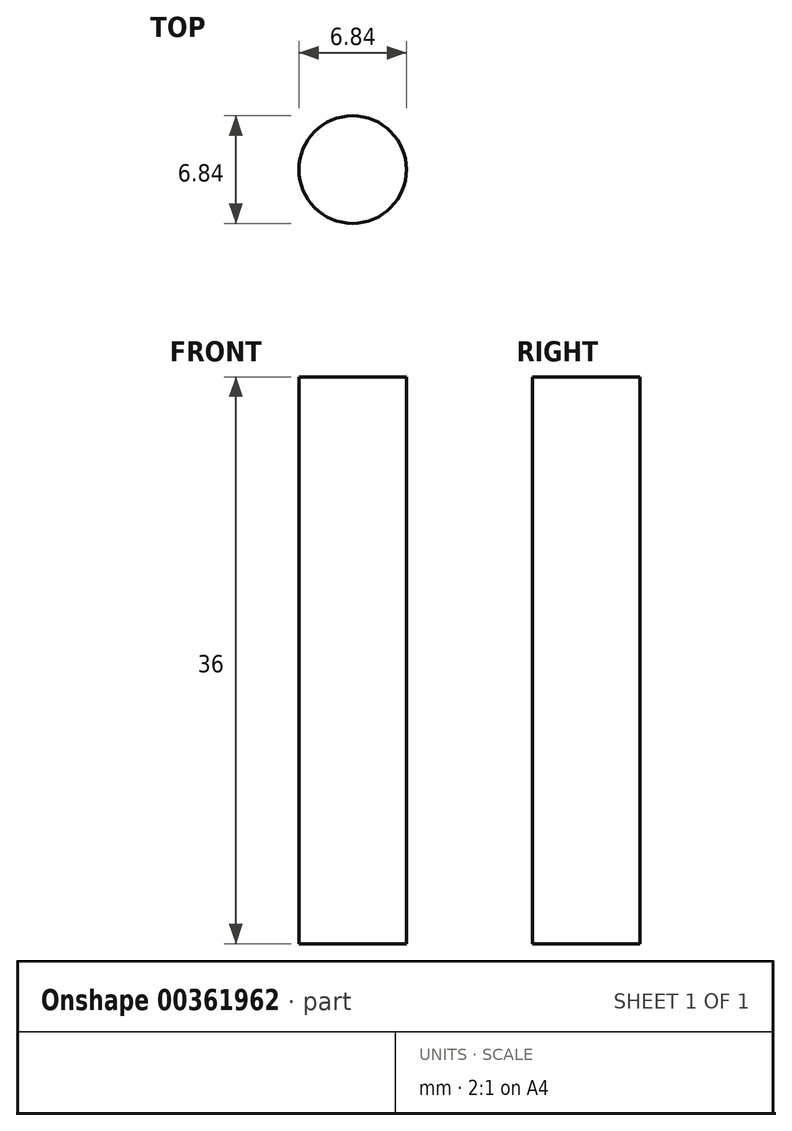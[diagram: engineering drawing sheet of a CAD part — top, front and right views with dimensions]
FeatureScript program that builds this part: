
annotation { "Feature Type Name" : "Feature", "Feature Type Description" : "" }
export const myFeature = defineFeature(function(context is Context, id is Id, definition is map)
    precondition{}
    {
        {
            var Q0;
            Q0=qCreatedBy(makeId("Top.planeOp"),FACE);
            var sketch = newSketch(context, id + "F0", { "sketchPlane" : qUnion([Q0])});
            skCircle(sketch, "E0", {"center": v(0, 0) * mm, "radius": 3.42 * mm});
            skSolve(sketch);
        }
        {
            var Q0;
            Q0 = qSketchRegion(id + "F0", true);
            extrude(context, id + "F1", {"entities" : qUnion([Q0]), "depth" : 36 * mm});
        }
    });
